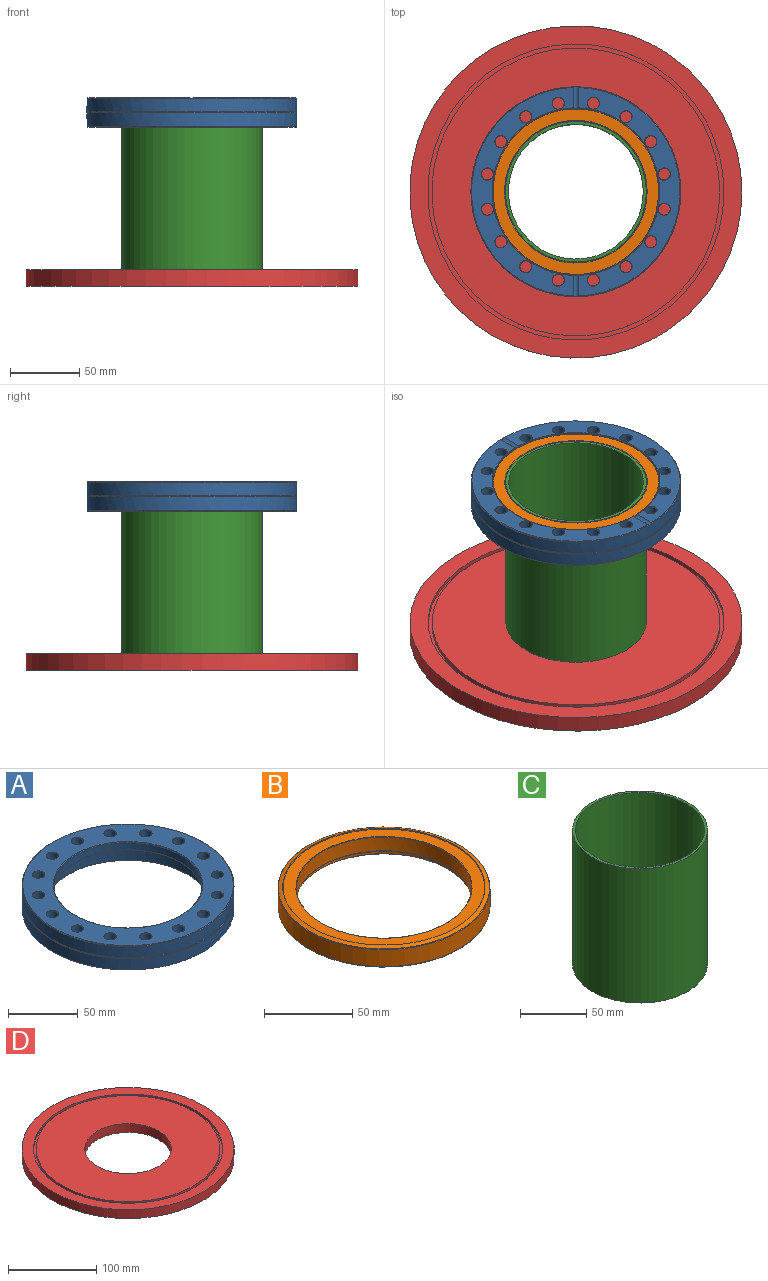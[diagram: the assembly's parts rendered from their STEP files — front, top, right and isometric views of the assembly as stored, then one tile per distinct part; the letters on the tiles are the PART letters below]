
ASSEMBLY  parts=4 mates=5
PART A: 67 faces, bbox 164.7x164.7x21.3 mm
  f0: plane 150.58x73.54mm, normal (0,0,-1), area 2585.5mm2, adj f1,f7,f39,f42,f45,f48,f51,f54
  f1: cylinder r=2.38mm len=15.48mm, axis (0,1,0), area 61.2mm2, adj f0,f2,f3,f5,f7,f8,f62,f64
  f2: cone r=75.31mm half-angle=45deg, axis (0,0,1), area 168.5mm2, adj f1,f3,f8,f61
  f3: plane 150.58x73.54mm, normal (0,0,-1), area 2585.5mm2, adj f1,f2,f15,f18,f21,f24,f27,f30
  f4: plane 150.62x150.62mm, normal (0,0,1), area 7790.1mm2, adj f12,f14,f17,f20,f23,f26,f29,f32
  f5: cylinder r=60.35mm len=120.7mm, axis (0,0,-1), area 5179.6mm2, adj f1,f61,f62,f64,f65
  f6: cylinder r=75.82mm len=151.64mm, axis (0,0,1), area 4630.5mm2, adj f11,f12
  f7: cone r=75.31mm half-angle=45deg, axis (0,0,1), area 168.5mm2, adj f0,f1,f8,f61
  f8: cylinder r=75.82mm len=151.64mm, axis (0,0,1), area 4630.5mm2, adj f1,f2,f7,f11,f61
  f9: cylinder r=53.09mm len=106.17mm, axis (0,0,1), area 2092.6mm2, adj f63,f66
  f10: plane 119.94x119.94mm, normal (0,0,-1), area 2359.9mm2, adj f63,f65
  f11: torus R=76.07mm, axis (0,0,1), area 505.7mm2, adj f6,f8
  f12: cone r=75.82mm half-angle=45deg, axis (0,0,-1), area 341.1mm2, adj f4,f6
  f13: cylinder r=4.22mm len=20.83mm, axis (0,0,1), area 551.8mm2, adj f14,f15
  f14: cone r=4.47mm half-angle=45deg, axis (0,0,1), area 9.8mm2, adj f4,f13
  f15: cone r=4.22mm half-angle=45deg, axis (0,0,-1), area 9.8mm2, adj f3,f13
  f16: cylinder r=4.22mm len=20.83mm, axis (0,0,1), area 551.8mm2, adj f17,f18
  f17: cone r=4.47mm half-angle=45deg, axis (0,0,1), area 9.8mm2, adj f4,f16
  f18: cone r=4.22mm half-angle=45deg, axis (0,0,-1), area 9.8mm2, adj f3,f16
  f19: cylinder r=4.22mm len=20.83mm, axis (0,0,1), area 551.8mm2, adj f20,f21
  f20: cone r=4.47mm half-angle=45deg, axis (0,0,1), area 9.8mm2, adj f4,f19
  f21: cone r=4.22mm half-angle=45deg, axis (0,0,-1), area 9.8mm2, adj f3,f19
  f22: cylinder r=4.22mm len=20.83mm, axis (0,0,1), area 551.8mm2, adj f23,f24
  f23: cone r=4.47mm half-angle=45deg, axis (0,0,1), area 9.8mm2, adj f4,f22
  f24: cone r=4.22mm half-angle=45deg, axis (0,0,-1), area 9.8mm2, adj f3,f22
  f25: cylinder r=4.22mm len=20.83mm, axis (0,0,1), area 551.8mm2, adj f26,f27
  f26: cone r=4.47mm half-angle=45deg, axis (0,0,1), area 9.8mm2, adj f4,f25
  f27: cone r=4.22mm half-angle=45deg, axis (0,0,-1), area 9.8mm2, adj f3,f25
  f28: cylinder r=4.22mm len=20.83mm, axis (0,0,1), area 551.8mm2, adj f29,f30
  f29: cone r=4.47mm half-angle=45deg, axis (0,0,1), area 9.8mm2, adj f4,f28
  f30: cone r=4.22mm half-angle=45deg, axis (0,0,-1), area 9.8mm2, adj f3,f28
  f31: cylinder r=4.22mm len=20.83mm, axis (0,0,1), area 551.8mm2, adj f32,f33
  f32: cone r=4.47mm half-angle=45deg, axis (0,0,1), area 9.8mm2, adj f4,f31
  f33: cone r=4.22mm half-angle=45deg, axis (0,0,-1), area 9.8mm2, adj f3,f31
  f34: cylinder r=4.22mm len=20.83mm, axis (0,0,1), area 551.8mm2, adj f35,f36
  f35: cone r=4.47mm half-angle=45deg, axis (0,0,1), area 9.8mm2, adj f4,f34
  f36: cone r=4.22mm half-angle=45deg, axis (0,0,-1), area 9.8mm2, adj f3,f34
  f37: cylinder r=4.22mm len=20.83mm, axis (0,0,1), area 551.8mm2, adj f38,f39
  f38: cone r=4.47mm half-angle=45deg, axis (0,0,1), area 9.8mm2, adj f4,f37
  f39: cone r=4.22mm half-angle=45deg, axis (0,0,-1), area 9.8mm2, adj f0,f37
  f40: cylinder r=4.22mm len=20.83mm, axis (0,0,1), area 551.8mm2, adj f41,f42
  f41: cone r=4.47mm half-angle=45deg, axis (0,0,1), area 9.8mm2, adj f4,f40
  f42: cone r=4.22mm half-angle=45deg, axis (0,0,-1), area 9.8mm2, adj f0,f40
  f43: cylinder r=4.22mm len=20.83mm, axis (0,0,1), area 551.8mm2, adj f44,f45
  f44: cone r=4.47mm half-angle=45deg, axis (0,0,1), area 9.8mm2, adj f4,f43
  f45: cone r=4.22mm half-angle=45deg, axis (0,0,-1), area 9.8mm2, adj f0,f43
  f46: cylinder r=4.22mm len=20.83mm, axis (0,0,1), area 551.8mm2, adj f47,f48
  f47: cone r=4.47mm half-angle=45deg, axis (0,0,1), area 9.8mm2, adj f4,f46
  f48: cone r=4.22mm half-angle=45deg, axis (0,0,-1), area 9.8mm2, adj f0,f46
  f49: cylinder r=4.22mm len=20.83mm, axis (0,0,1), area 551.8mm2, adj f50,f51
  f50: cone r=4.47mm half-angle=45deg, axis (0,0,1), area 9.8mm2, adj f4,f49
  f51: cone r=4.22mm half-angle=45deg, axis (0,0,-1), area 9.8mm2, adj f0,f49
  f52: cylinder r=4.22mm len=20.83mm, axis (0,0,1), area 551.8mm2, adj f53,f54
  f53: cone r=4.47mm half-angle=45deg, axis (0,0,1), area 9.8mm2, adj f4,f52
  f54: cone r=4.22mm half-angle=45deg, axis (0,0,-1), area 9.8mm2, adj f0,f52
  f55: cylinder r=4.22mm len=20.83mm, axis (0,0,1), area 551.8mm2, adj f56,f57
  f56: cone r=4.47mm half-angle=45deg, axis (0,0,1), area 9.8mm2, adj f4,f55
  f57: cone r=4.22mm half-angle=45deg, axis (0,0,-1), area 9.8mm2, adj f0,f55
  f58: cylinder r=4.22mm len=20.83mm, axis (0,0,1), area 551.8mm2, adj f59,f60
  f59: cone r=4.47mm half-angle=45deg, axis (0,0,1), area 9.8mm2, adj f4,f58
  f60: cone r=4.22mm half-angle=45deg, axis (0,0,-1), area 9.8mm2, adj f0,f58
  f61: cylinder r=2.38mm len=15.48mm, axis (0,-1,0), area 61.2mm2, adj f0,f2,f3,f5,f7,f8,f62,f64
  f62: torus R=60.6mm, axis (0,0,-1), area 74.5mm2, adj f0,f1,f5,f61
  f63: torus R=53.34mm, axis (0,0,1), area 133.3mm2, adj f9,f10
  f64: torus R=60.6mm, axis (0,0,-1), area 74.5mm2, adj f1,f3,f5,f61
  f65: torus R=59.97mm, axis (0,0,1), area 226.4mm2, adj f5,f10
  f66: torus R=53.59mm, axis (0,0,-1), area 267.1mm2, adj f4,f9
PART B: 15 faces, bbox 130.4x130.4x13.6 mm
  f0: cylinder r=51.05mm len=102.11mm, axis (0,0,-1), area 510.8mm2, adj f2,f14
  f1: cylinder r=60.25mm len=120.5mm, axis (0,0,1), area 4486.9mm2, adj f8,f9
  f2: cone r=51.05mm half-angle=32deg, axis (0,0,1), area 196.2mm2, adj f0,f3
  f3: torus R=51.05mm, axis (0,0,1), area 261.6mm2, adj f2,f4
  f4: plane 102.11x102.11mm, normal (0,0,-1), area 338.6mm2, adj f3,f5
  f5: torus R=49.99mm, axis (0,0,1), area 100mm2, adj f4,f13
  f6: torus R=50.04mm, axis (0,0,-1), area 125mm2, adj f11,f13
  f7: plane 119.48x119.48mm, normal (0,0,-1), area 2859.9mm2, adj f8,f14
  f8: torus R=59.74mm, axis (0,0,-1), area 301.1mm2, adj f1,f7
  f9: torus R=59.87mm, axis (0,0,-1), area 176mm2, adj f1,f12
  f10: cone r=57.47mm half-angle=20deg, axis (0,0,1), area 194.9mm2, adj f11,f12
  f11: plane 114.57x114.57mm, normal (0,0,1), area 2442.6mm2, adj f6,f10
  f12: cone r=60.32mm half-angle=70deg, axis (0,0,-1), area 993.8mm2, adj f9,f10
  f13: cylinder r=49.78mm len=99.57mm, axis (0,0,1), area 2963.5mm2, adj f5,f6
  f14: cone r=51.56mm half-angle=45deg, axis (0,0,-1), area 231.6mm2, adj f0,f7
PART C: 4 faces, bbox 101.6x101.6x123.8 mm
  f0: cylinder r=50.8mm len=123.77mm, axis (0,0,1), area 39507mm2, adj f2,f3
  f1: cylinder r=48.69mm len=123.77mm, axis (0,0,1), area 37867.4mm2, adj f2,f3
  f2: plane 101.6x101.6mm, normal (0,0,-1), area 658.9mm2, adj f0,f1
  f3: plane 101.6x101.6mm, normal (0,0,1), area 658.9mm2, adj f0,f1
PART D: 8 faces, bbox 240x240x12 mm
  f0: cylinder r=120mm len=240mm, axis (0,0,-1), area 9047.8mm2, adj f1,f2
  f1: plane 240x240mm, normal (0,0,1), area 9270.8mm2, adj f0,f4
  f2: plane 240x240mm, normal (0,0,-1), area 37726.7mm2, adj f0,f7
  f3: cylinder r=104mm len=208mm, axis (0,0,1), area 1960.4mm2, adj f5,f6
  f4: cylinder r=107mm len=214mm, axis (0,0,1), area 2016.9mm2, adj f1,f5
  f5: plane 214x214mm, normal (0,0,1), area 1988.6mm2, adj f3,f4
  f6: plane 208x208mm, normal (0,0,1), area 26467.3mm2, adj f3,f7
  f7: cylinder r=48.9mm len=97.8mm, axis (0,0,1), area 3687mm2, adj f2,f6
PLACE A rot(axis=(0,1,0),180deg) t=(-1.01,0.37,119.65)mm
PLACE B rot(axis=(0,1,0),180deg) t=(-1.01,0.37,122.84)mm
PLACE C rot(axis=(0,1,0),180deg) t=(-1.01,0.37,67.77)mm
PLACE D t=(-1.01,0.37,-6.12)mm
MATE parallel C.f0 <-> D.f7  axis (0,0,-1) through (-1.01,0.37,5.88)mm
MATE slider B.f0 <-> C.f0  axis (0,0,1) through (-1.01,0.37,126.25)mm
MATE slider A.f5 <-> C.f0  axis (0,0,1) through (-1.01,0.37,115.76)mm
MATE parallel A.f5 <-> B.f2  axis (0,0,1) through (-1.01,0.37,116.02)mm
MATE parallel B.f0 <-> C.f0  axis (0,0,1) through (-1.01,0.37,129.66)mm
